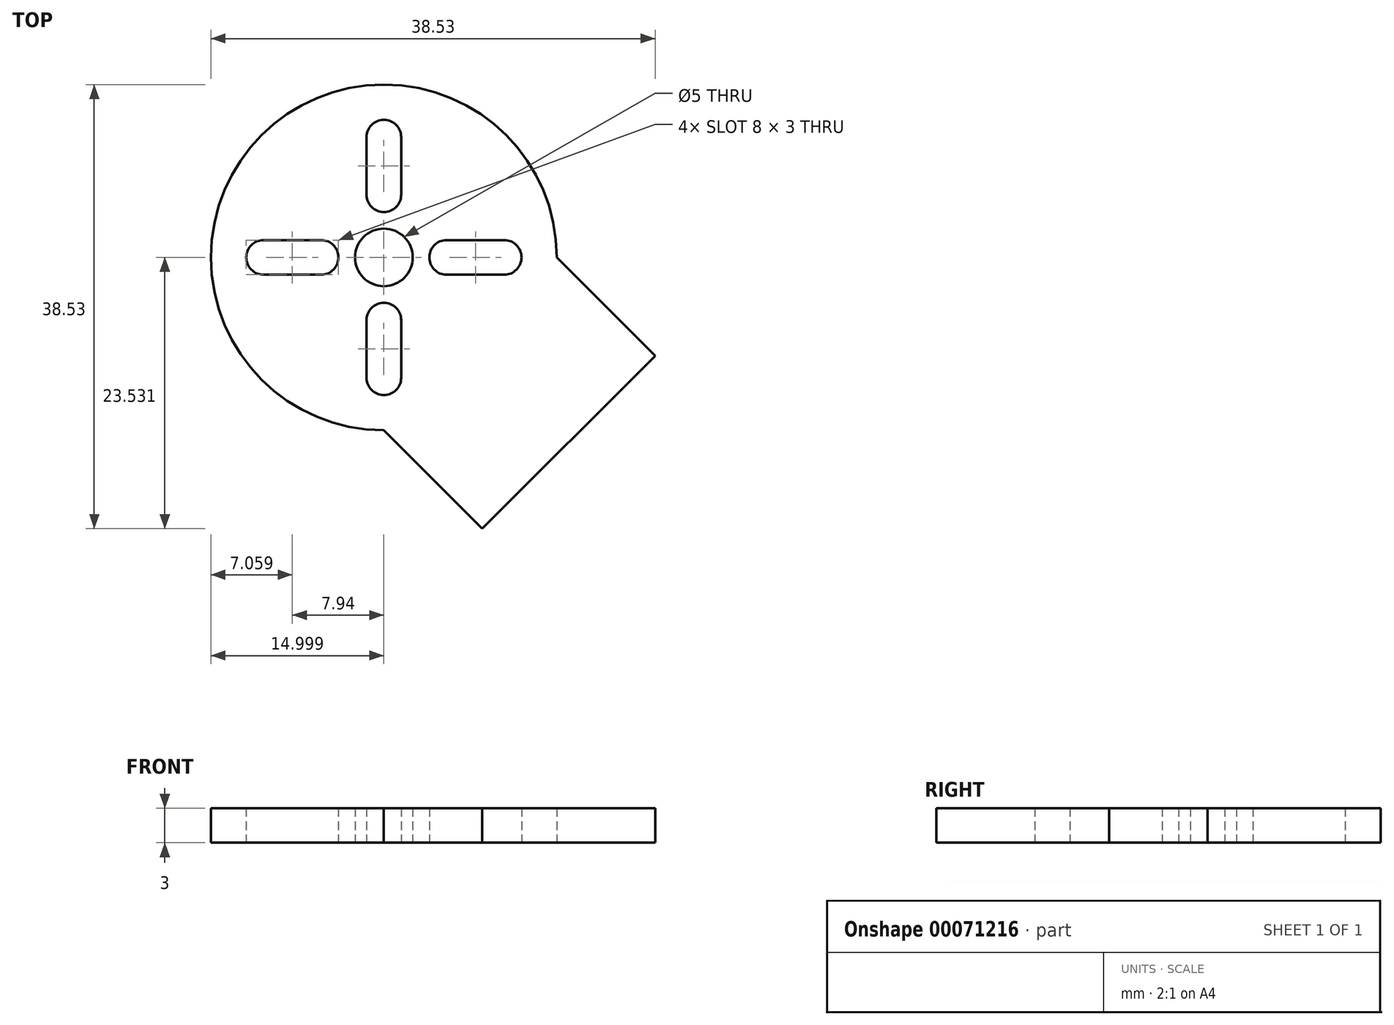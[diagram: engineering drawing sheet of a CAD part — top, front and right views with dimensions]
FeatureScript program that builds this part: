
annotation { "Feature Type Name" : "Feature", "Feature Type Description" : "" }
export const myFeature = defineFeature(function(context is Context, id is Id, definition is map)
    precondition{}
    {
        {
            var Q0;
            Q0=qCreatedBy(makeId("Top.planeOp"),FACE);
            var sketch = newSketch(context, id + "F0", { "sketchPlane" : qUnion([Q0])});
            skLineSegment(sketch, "E0.rect.right", {"start": v(-70.71, -70.71) * mm, "end": v(-70.71, 70.71) * mm, "construction": true});
            skArc(sketch, "E1", {"start": v(-55.71, 70.71) * mm, "mid": v(-81.32, 81.32) * mm, "end": v(-70.71, 55.71) * mm});
            skLineSegment(sketch, "E2", {"start": v(70.71, 70.71) * mm, "end": v(-70.71, -70.71) * mm, "construction": true});
            skLineSegment(sketch, "E3", {"start": v(70.71, -70.71) * mm, "end": v(-70.71, 70.71) * mm, "construction": true});
            skCircle(sketch, "E4", {"center": v(-70.71, 70.71) * mm, "radius": 2.5 * mm});
            skLineSegment(sketch, "E5.rect.left", {"start": v(-69.21, 76.15) * mm, "end": v(-69.21, 81.15) * mm});
            skLineSegment(sketch, "E5.rect.right", {"start": v(-72.21, 76.15) * mm, "end": v(-72.21, 81.15) * mm});
            skArc(sketch, "E6", {"start": v(-69.21, 81.15) * mm, "mid": v(-70.71, 82.65) * mm, "end": v(-72.21, 81.15) * mm});
            skArc(sketch, "E7", {"start": v(-72.21, 76.15) * mm, "mid": v(-70.71, 74.65) * mm, "end": v(-69.21, 76.15) * mm});
            skLineSegment(sketch, "E8", {"start": v(-70.71, 70.71) * mm, "end": v(70.71, 70.71) * mm, "construction": true});
            skLineSegment(sketch, "E9", {"start": v(-70.71, 70.71) * mm, "end": v(-68.94, 72.48) * mm});
            skLineSegment(sketch, "E10", {"start": v(-70.71, 70.71) * mm, "end": v(-72.48, 68.94) * mm});
            skLineSegment(sketch, "E11.MirrorCS", {"start": v(-69.21, 65.27) * mm, "end": v(-69.21, 60.27) * mm});
            skArc(sketch, "E12.MirrorCS", {"start": v(-69.21, 60.27) * mm, "mid": v(-70.71, 58.77) * mm, "end": v(-72.21, 60.27) * mm});
            skLineSegment(sketch, "E13.MirrorCS", {"start": v(-72.21, 65.27) * mm, "end": v(-72.21, 60.27) * mm});
            skArc(sketch, "E14.MirrorCS", {"start": v(-72.21, 65.27) * mm, "mid": v(-70.71, 66.77) * mm, "end": v(-69.21, 65.27) * mm});
            skLineSegment(sketch, "E15.MirrorCS", {"start": v(-65.27, 69.21) * mm, "end": v(-60.27, 69.21) * mm});
            skArc(sketch, "E16.MirrorCS", {"start": v(-65.27, 72.21) * mm, "mid": v(-66.77, 70.71) * mm, "end": v(-65.27, 69.21) * mm});
            skLineSegment(sketch, "E17.MirrorCS", {"start": v(-65.27, 72.21) * mm, "end": v(-60.27, 72.21) * mm});
            skArc(sketch, "E18.MirrorCS", {"start": v(-60.27, 69.21) * mm, "mid": v(-58.77, 70.71) * mm, "end": v(-60.27, 72.21) * mm});
            skLineSegment(sketch, "E19.MirrorCS", {"start": v(-76.15, 69.21) * mm, "end": v(-81.15, 69.21) * mm});
            skArc(sketch, "E20.MirrorCS", {"start": v(-76.15, 69.21) * mm, "mid": v(-74.65, 70.71) * mm, "end": v(-76.15, 72.21) * mm});
            skLineSegment(sketch, "E21.MirrorCS", {"start": v(-76.15, 72.21) * mm, "end": v(-81.15, 72.21) * mm});
            skArc(sketch, "E22.MirrorCS", {"start": v(-81.15, 72.21) * mm, "mid": v(-82.65, 70.71) * mm, "end": v(-81.15, 69.21) * mm});
            skLineSegment(sketch, "E23", {"start": v(-62.18, 47.18) * mm, "end": v(-47.18, 62.18) * mm});
            skLineSegment(sketch, "E24", {"start": v(-55.71, 70.71) * mm, "end": v(-47.18, 62.18) * mm});
            skLineSegment(sketch, "E25", {"start": v(-70.71, 55.71) * mm, "end": v(-62.18, 47.18) * mm});
            skSolve(sketch);
        }
        {
            var Q0;
            Q0=makeQuery(id+"F0.imprint","IMPRINT",FACE,{"disambiguationData":[TD([[makeQuery(id+"F0.imprint","IMPRINT",EDGE,{"derivedFrom":sQuery(id+"F0.wireOp",EDGE,"E1")}),1.0]])]});
            extrude(context, id + "F1", {"entities" : qUnion([Q0]), "depth" : 3 * mm});
        }
    });
